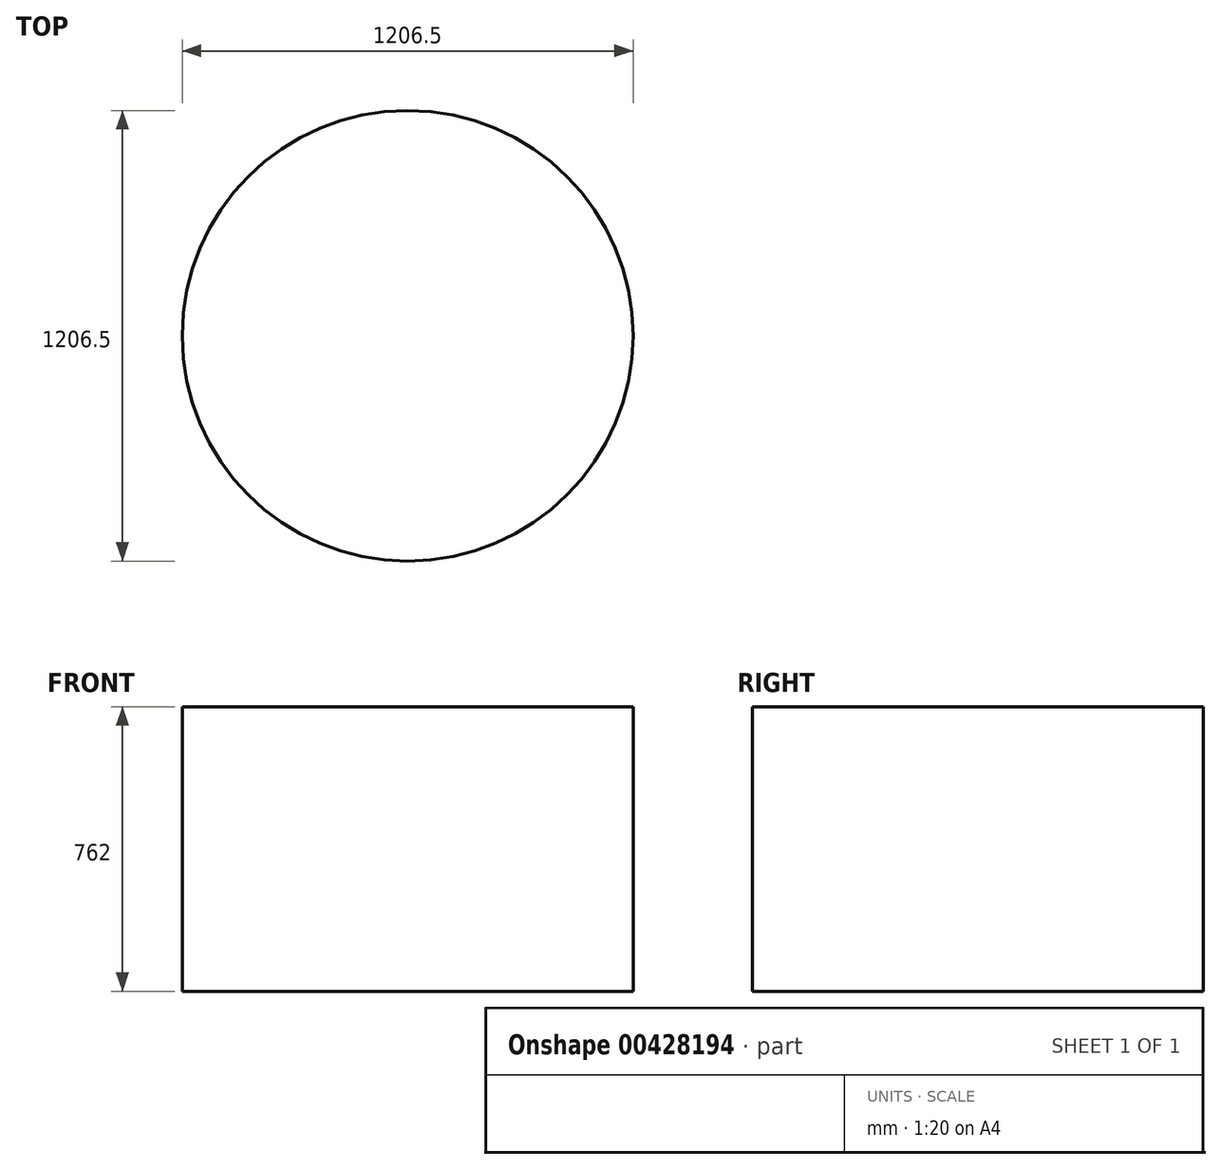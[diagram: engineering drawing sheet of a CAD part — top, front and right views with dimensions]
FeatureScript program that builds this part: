
annotation { "Feature Type Name" : "Feature", "Feature Type Description" : "" }
export const myFeature = defineFeature(function(context is Context, id is Id, definition is map)
    precondition{}
    {
        {
            var Q0;
            Q0=qCreatedBy(makeId("Top.planeOp"),FACE);
            var sketch = newSketch(context, id + "F0", { "sketchPlane" : qUnion([Q0])});
            skCircle(sketch, "E0", {"center": v(0, 0) * mm, "radius": 603.25 * mm});
            skSolve(sketch);
        }
        {
            var Q0;
            Q0=makeQuery(id+"F0.imprint","IMPRINT",FACE,{"disambiguationData":[TD([[makeQuery(id+"F0.imprint","IMPRINT",EDGE,{"derivedFrom":sQuery(id+"F0.wireOp",EDGE,"E0")}),1.0]])]});
            extrude(context, id + "F1", {"entities" : qUnion([Q0]), "depth" : 762 * mm});
        }
    });
